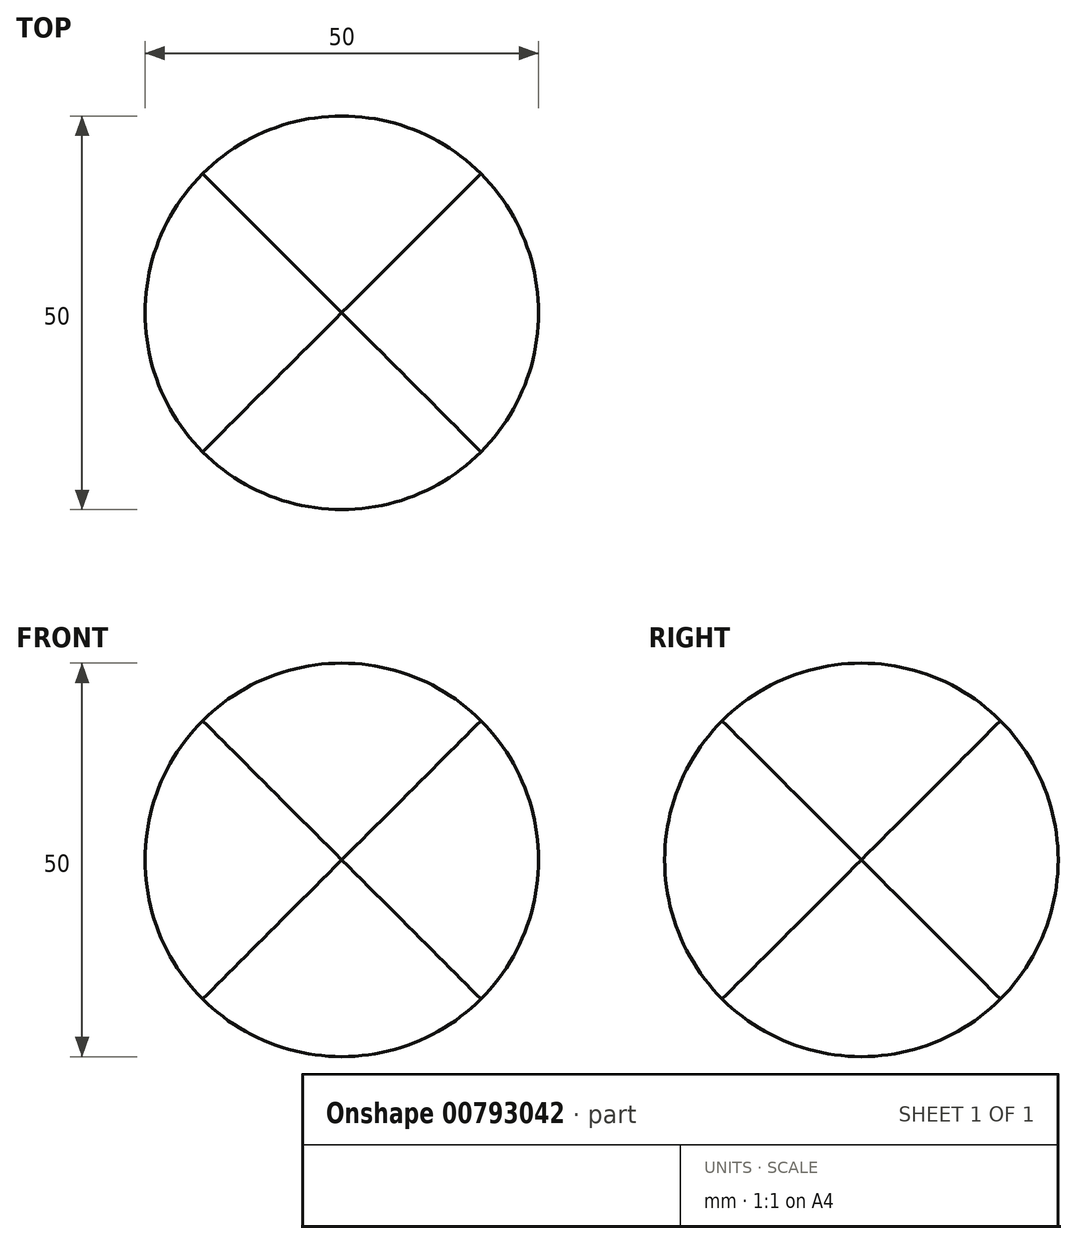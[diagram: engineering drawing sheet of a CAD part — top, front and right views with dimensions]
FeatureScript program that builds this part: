
annotation { "Feature Type Name" : "Feature", "Feature Type Description" : "" }
export const myFeature = defineFeature(function(context is Context, id is Id, definition is map)
    precondition{}
    {
        {
            var Q0;
            Q0=qCreatedBy(makeId("Top.planeOp"),FACE);
            var sketch = newSketch(context, id + "F0", { "sketchPlane" : qUnion([Q0])});
            skLineSegment(sketch, "E0.bottom", {"start": v(25, -25) * mm, "end": v(-25, -25) * mm});
            skLineSegment(sketch, "E0.top", {"start": v(25, 25) * mm, "end": v(-25, 25) * mm});
            skLineSegment(sketch, "E0.left", {"start": v(25, -25) * mm, "end": v(25, 25) * mm});
            skLineSegment(sketch, "E0.right", {"start": v(-25, -25) * mm, "end": v(-25, 25) * mm});
            skPoint(sketch, "E0.middle", {"position": v(0, 0) * mm});
            skSolve(sketch);
        }
        {
            var Q0;
            Q0 = qSketchRegion(id + "F0", true);
            extrude(context, id + "F1", {"entities" : qUnion([Q0]), "depth" : 50 * mm, "offsetDistance" : 25 * mm});
        }
        {
            var Q0;
            Q0=makeQuery(id+"F1.opExtrude","SWEPT_FACE",FACE,{"disambiguationData":[OSD([sQuery(id+"F0.wireOp",EDGE,"E0.bottom")])]});
            var sketch = newSketch(context, id + "F2", { "sketchPlane" : qUnion([Q0])});
            skCircle(sketch, "E1", {"center": v(0, 25) * mm, "radius": 25 * mm});
            skPoint(sketch, "E1.centerSnap0", {"position": v(25, 25) * mm});
            skSolve(sketch);
        }
        {
            var Q0;
            Q0=makeQuery(id+"F1.opExtrude","CAP_FACE",FACE,{"disambiguationData":[OSD([sQuery(id+"F0.wireOp",EDGE,"E0.bottom"),sQuery(id+"F0.wireOp",EDGE,"E0.top"),sQuery(id+"F0.wireOp",EDGE,"E0.left"),sQuery(id+"F0.wireOp",EDGE,"E0.right")])],"isStart":false});
            var sketch = newSketch(context, id + "F3", { "sketchPlane" : qUnion([Q0])});
            skCircle(sketch, "E2", {"center": v(0, 0) * mm, "radius": 25 * mm});
            skSolve(sketch);
        }
        {
            var Q0;
            Q0=makeQuery(id+"F1.opExtrude","SWEPT_FACE",FACE,{"disambiguationData":[OSD([sQuery(id+"F0.wireOp",EDGE,"E0.left")])]});
            var sketch = newSketch(context, id + "F4", { "sketchPlane" : qUnion([Q0])});
            skCircle(sketch, "E3", {"center": v(0, 25) * mm, "radius": 25 * mm});
            skPoint(sketch, "E3.centerSnap0", {"position": v(-25, 25) * mm});
            skSolve(sketch);
        }
        {
            var Q0;
            {var subQ0=sQuery(id+"F2.wireOp",EDGE,"E1");var subQ1=sQuery(id+"F0.wireOp",EDGE,"E0.bottom");var subQ2=makeQuery(id+"F1.opExtrude","CAP_EDGE",EDGE,{"disambiguationData":[OSD([subQ1])],"isStart":false});var subQ3=makeQuery(id+"F2.imprint","INTERSECT",VERTEX,{"derivedFrom":[subQ2,subQ0]});Q0=makeQuery(id+"F2.imprint","IMPRINT",FACE,{"disambiguationData":[TD([[makeQuery(id+"F2.imprint","IMPRINT",EDGE,{"disambiguationData":[TD([[subQ3,1.0]])],"derivedFrom":subQ0}),-1.0]])]});}
            var Q1;
            {var subQ0=sQuery(id+"F2.wireOp",EDGE,"E1");var subQ1=sQuery(id+"F0.wireOp",EDGE,"E0.bottom");var subQ4=makeQuery(id+"F1.opExtrude","CAP_EDGE",EDGE,{"disambiguationData":[OSD([subQ1])],"isStart":true});var subQ5=makeQuery(id+"F2.imprint","INTERSECT",VERTEX,{"derivedFrom":[subQ4,subQ0]});Q1=makeQuery(id+"F2.imprint","IMPRINT",FACE,{"disambiguationData":[TD([[makeQuery(id+"F2.imprint","IMPRINT",EDGE,{"disambiguationData":[TD([[subQ5,-1.0]])],"derivedFrom":subQ0}),-1.0]])]});}
            var Q2;
            {var subQ0=sQuery(id+"F2.wireOp",EDGE,"E1");var subQ1=sQuery(id+"F0.wireOp",EDGE,"E0.bottom");var subQ4=makeQuery(id+"F1.opExtrude","CAP_EDGE",EDGE,{"disambiguationData":[OSD([subQ1])],"isStart":true});var subQ5=makeQuery(id+"F2.imprint","INTERSECT",VERTEX,{"derivedFrom":[subQ4,subQ0]});Q2=makeQuery(id+"F2.imprint","IMPRINT",FACE,{"disambiguationData":[TD([[makeQuery(id+"F2.imprint","IMPRINT",EDGE,{"disambiguationData":[TD([[subQ5,1.0]])],"derivedFrom":subQ0}),-1.0]])]});}
            var Q3;
            {var subQ0=sQuery(id+"F2.wireOp",EDGE,"E1");var subQ1=sQuery(id+"F0.wireOp",EDGE,"E0.bottom");var subQ2=makeQuery(id+"F1.opExtrude","CAP_EDGE",EDGE,{"disambiguationData":[OSD([subQ1])],"isStart":false});var subQ3=makeQuery(id+"F2.imprint","INTERSECT",VERTEX,{"derivedFrom":[subQ2,subQ0]});Q3=makeQuery(id+"F2.imprint","IMPRINT",FACE,{"disambiguationData":[TD([[makeQuery(id+"F2.imprint","IMPRINT",EDGE,{"disambiguationData":[TD([[subQ3,-1.0]])],"derivedFrom":subQ0}),-1.0]])]});}
            extrude(context, id + "F5", {"entities" : qUnion([Q0, Q1, Q2, Q3]), "operationType" : NewBodyOperationType.REMOVE, "oppositeDirection" : true, "depth" : 60 * mm, "offsetDistance" : 25 * mm});
        }
        {
            var Q0;
            {var subQ0=sQuery(id+"F4.wireOp",EDGE,"E3");var subQ1=sQuery(id+"F0.wireOp",EDGE,"E0.left");var subQ2=makeQuery(id+"F1.opExtrude","CAP_EDGE",EDGE,{"disambiguationData":[OSD([subQ1])],"isStart":false});var subQ3=makeQuery(id+"F4.imprint","INTERSECT",VERTEX,{"derivedFrom":[subQ2,subQ0]});Q0=makeQuery(id+"F4.imprint","IMPRINT",FACE,{"disambiguationData":[TD([[makeQuery(id+"F4.imprint","IMPRINT",EDGE,{"disambiguationData":[TD([[subQ3,-1.0]])],"derivedFrom":subQ0}),-1.0]])]});}
            var Q1;
            {var subQ0=sQuery(id+"F4.wireOp",EDGE,"E3");var subQ1=sQuery(id+"F0.wireOp",EDGE,"E0.left");var subQ2=makeQuery(id+"F1.opExtrude","CAP_EDGE",EDGE,{"disambiguationData":[OSD([subQ1])],"isStart":false});var subQ3=makeQuery(id+"F4.imprint","INTERSECT",VERTEX,{"derivedFrom":[subQ2,subQ0]});Q1=makeQuery(id+"F4.imprint","IMPRINT",FACE,{"disambiguationData":[TD([[makeQuery(id+"F4.imprint","IMPRINT",EDGE,{"disambiguationData":[TD([[subQ3,1.0]])],"derivedFrom":subQ0}),-1.0]])]});}
            var Q2;
            {var subQ0=sQuery(id+"F4.wireOp",EDGE,"E3");var subQ1=sQuery(id+"F0.wireOp",EDGE,"E0.left");var subQ4=makeQuery(id+"F1.opExtrude","CAP_EDGE",EDGE,{"disambiguationData":[OSD([subQ1])],"isStart":true});var subQ5=makeQuery(id+"F4.imprint","INTERSECT",VERTEX,{"derivedFrom":[subQ4,subQ0]});Q2=makeQuery(id+"F4.imprint","IMPRINT",FACE,{"disambiguationData":[TD([[makeQuery(id+"F4.imprint","IMPRINT",EDGE,{"disambiguationData":[TD([[subQ5,-1.0]])],"derivedFrom":subQ0}),-1.0]])]});}
            var Q3;
            {var subQ0=sQuery(id+"F4.wireOp",EDGE,"E3");var subQ1=sQuery(id+"F0.wireOp",EDGE,"E0.left");var subQ4=makeQuery(id+"F1.opExtrude","CAP_EDGE",EDGE,{"disambiguationData":[OSD([subQ1])],"isStart":true});var subQ5=makeQuery(id+"F4.imprint","INTERSECT",VERTEX,{"derivedFrom":[subQ4,subQ0]});Q3=makeQuery(id+"F4.imprint","IMPRINT",FACE,{"disambiguationData":[TD([[makeQuery(id+"F4.imprint","IMPRINT",EDGE,{"disambiguationData":[TD([[subQ5,1.0]])],"derivedFrom":subQ0}),-1.0]])]});}
            extrude(context, id + "F6", {"entities" : qUnion([Q0, Q1, Q2, Q3]), "operationType" : NewBodyOperationType.REMOVE, "oppositeDirection" : true, "depth" : 60 * mm, "offsetDistance" : 25 * mm});
        }
        {
            var Q0;
            {var subQ0=sQuery(id+"F3.wireOp",EDGE,"E2");var subQ1=makeQuery(id+"F1.opExtrude","CAP_EDGE",EDGE,{"disambiguationData":[OSD([sQuery(id+"F0.wireOp",EDGE,"E0.left")])],"isStart":false});var subQ2=makeQuery(id+"F3.imprint","INTERSECT",VERTEX,{"derivedFrom":[subQ1,subQ0]});Q0=makeQuery(id+"F3.imprint","IMPRINT",FACE,{"disambiguationData":[TD([[makeQuery(id+"F3.imprint","IMPRINT",EDGE,{"disambiguationData":[TD([[subQ2,1.0]])],"derivedFrom":subQ0}),-1.0]])]});}
            var Q1;
            {var subQ0=sQuery(id+"F3.wireOp",EDGE,"E2");var subQ1=makeQuery(id+"F1.opExtrude","CAP_EDGE",EDGE,{"disambiguationData":[OSD([sQuery(id+"F0.wireOp",EDGE,"E0.right")])],"isStart":false});var subQ2=makeQuery(id+"F3.imprint","INTERSECT",VERTEX,{"derivedFrom":[subQ1,subQ0]});Q1=makeQuery(id+"F3.imprint","IMPRINT",FACE,{"disambiguationData":[TD([[makeQuery(id+"F3.imprint","IMPRINT",EDGE,{"disambiguationData":[TD([[subQ2,-1.0]])],"derivedFrom":subQ0}),-1.0]])]});}
            var Q2;
            {var subQ0=sQuery(id+"F3.wireOp",EDGE,"E2");var subQ1=makeQuery(id+"F1.opExtrude","CAP_EDGE",EDGE,{"disambiguationData":[OSD([sQuery(id+"F0.wireOp",EDGE,"E0.top")])],"isStart":false});var subQ2=makeQuery(id+"F3.imprint","INTERSECT",VERTEX,{"derivedFrom":[subQ1,subQ0]});Q2=makeQuery(id+"F3.imprint","IMPRINT",FACE,{"disambiguationData":[TD([[makeQuery(id+"F3.imprint","IMPRINT",EDGE,{"disambiguationData":[TD([[subQ2,-1.0]])],"derivedFrom":subQ0}),-1.0]])]});}
            var Q3;
            {var subQ0=sQuery(id+"F3.wireOp",EDGE,"E2");var subQ1=makeQuery(id+"F1.opExtrude","CAP_EDGE",EDGE,{"disambiguationData":[OSD([sQuery(id+"F0.wireOp",EDGE,"E0.top")])],"isStart":false});var subQ2=makeQuery(id+"F3.imprint","INTERSECT",VERTEX,{"derivedFrom":[subQ1,subQ0]});Q3=makeQuery(id+"F3.imprint","IMPRINT",FACE,{"disambiguationData":[TD([[makeQuery(id+"F3.imprint","IMPRINT",EDGE,{"disambiguationData":[TD([[subQ2,1.0]])],"derivedFrom":subQ0}),-1.0]])]});}
            extrude(context, id + "F7", {"entities" : qUnion([Q0, Q1, Q2, Q3]), "operationType" : NewBodyOperationType.REMOVE, "oppositeDirection" : true, "depth" : 60 * mm, "offsetDistance" : 25 * mm});
        }
    });
